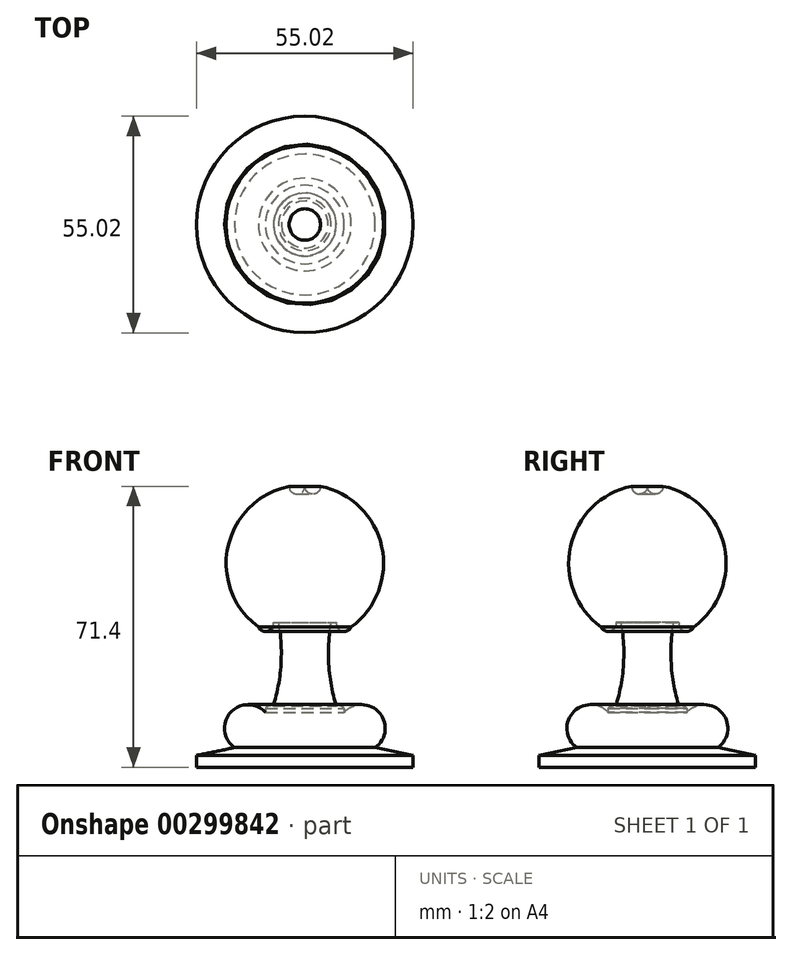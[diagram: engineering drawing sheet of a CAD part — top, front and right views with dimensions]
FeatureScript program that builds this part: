
annotation { "Feature Type Name" : "Feature", "Feature Type Description" : "" }
export const myFeature = defineFeature(function(context is Context, id is Id, definition is map)
    precondition{}
    {
        {
            var Q0;
            Q0=qCreatedBy(makeId("Front.planeOp"),FACE);
            var sketch = newSketch(context, id + "F0", { "sketchPlane" : qUnion([Q0])});
            skArc(sketch, "E0", {"start": v(4, 0) * mm, "mid": v(2, 2) * mm, "end": v(0, 0) * mm});
            skArc(sketch, "E1", {"start": v(11.78, -35.76) * mm, "mid": v(19.54, -15.34) * mm, "end": v(4, 0) * mm});
            skArc(sketch, "E2", {"start": v(8, -34.6) * mm, "mid": v(9.4, -36.8) * mm, "end": v(11.78, -35.76) * mm});
            skLineSegment(sketch, "E3", {"start": v(8, -34.6) * mm, "end": v(6.67, -34.6) * mm});
            skArc(sketch, "E4", {"start": v(6.67, -34.6) * mm, "mid": v(6.07, -45.27) * mm, "end": v(8, -55.76) * mm});
            skArc(sketch, "E5", {"start": v(10, -56.43) * mm, "mid": v(9.1, -55.81) * mm, "end": v(8, -55.76) * mm});
            skLineSegment(sketch, "E6", {"start": v(10, -56.43) * mm, "end": v(10, -57.43) * mm});
            skArc(sketch, "E7", {"start": v(17.86, -66.4) * mm, "mid": v(18.94, -57.53) * mm, "end": v(10, -57.43) * mm});
            skLineSegment(sketch, "E8", {"start": v(17.86, -66.4) * mm, "end": v(27.5, -68.4) * mm});
            skLineSegment(sketch, "E9", {"start": v(27.5, -68.4) * mm, "end": v(27.5, -71.4) * mm});
            skLineSegment(sketch, "E10", {"start": v(27.5, -71.4) * mm, "end": v(0, -71.4) * mm});
            skLineSegment(sketch, "E11", {"start": v(0, -71.4) * mm, "end": v(0, 0) * mm});
            skSolve(sketch);
        }
        {
            var Q0;
            Q0 = qSketchRegion(id + "F0", true);
            var Q1;
            Q1=makeQuery(id+"F0.imprint","IMPRINT",FACE,{"disambiguationData":[TD([[makeQuery(id+"F0.imprint","IMPRINT",EDGE,{"derivedFrom":sQuery(id+"F0.wireOp",EDGE,"E0")}),1.0]])]});
            var Q2;
            Q2=sQuery(id+"F0.wireOp",EDGE,"E11");
            revolve(context, id + "F1", {"entities" : qUnion([Q0, Q1]), "axis" : qUnion([Q2]), "revolveType" : RevolveType.FULL});
        }
    });
